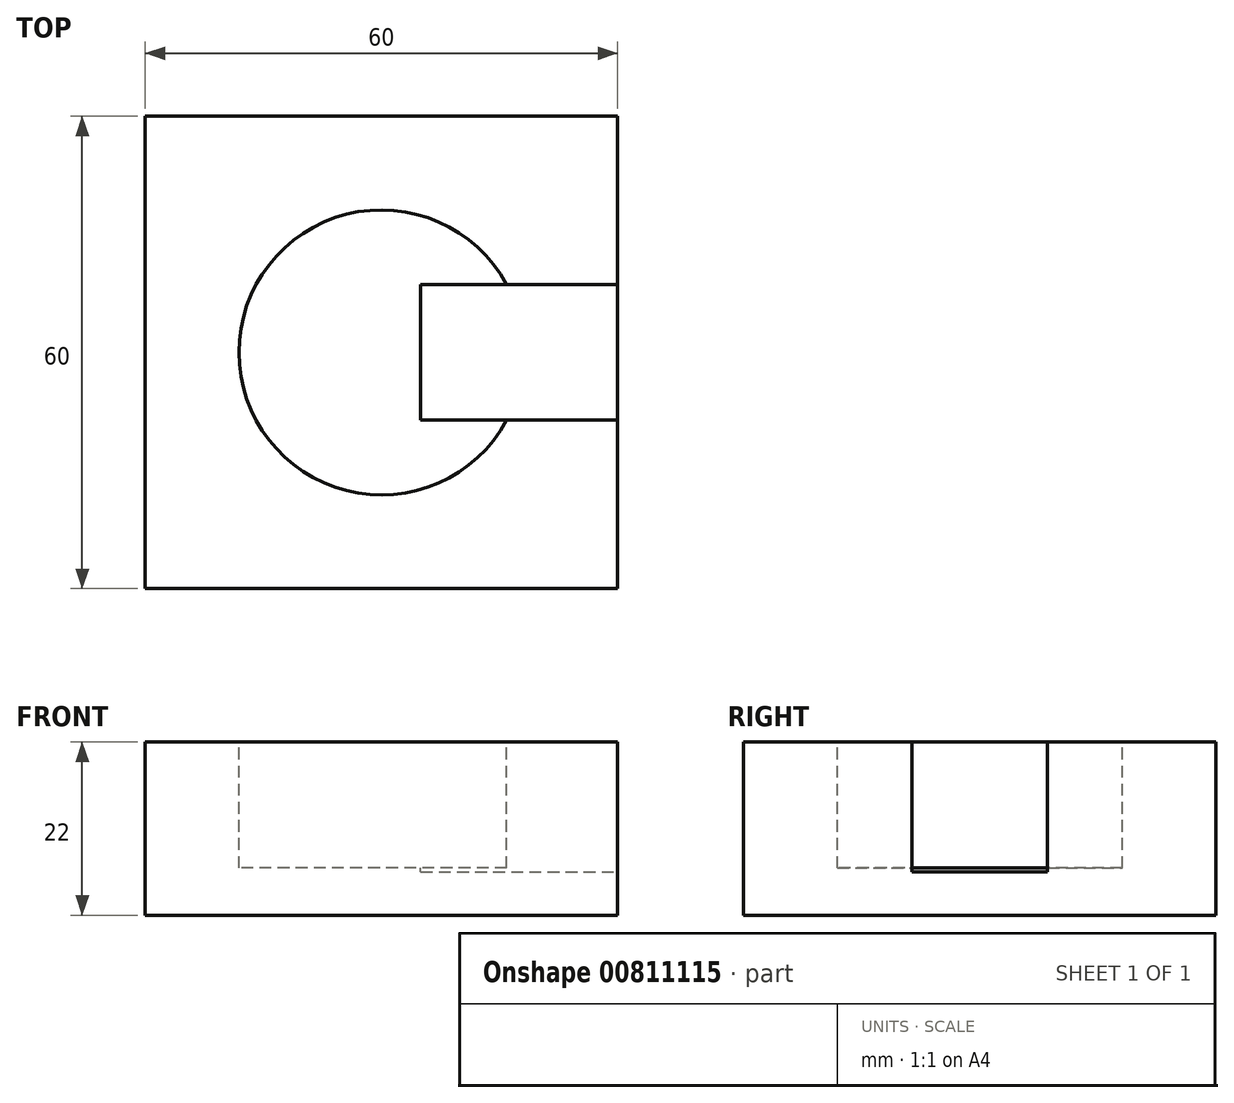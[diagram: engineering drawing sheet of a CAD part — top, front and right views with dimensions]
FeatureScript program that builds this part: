
annotation { "Feature Type Name" : "Feature", "Feature Type Description" : "" }
export const myFeature = defineFeature(function(context is Context, id is Id, definition is map)
    precondition{}
    {
        {
            var Q0;
            Q0=qCreatedBy(makeId("Top.planeOp"),FACE);
            var sketch = newSketch(context, id + "F0", { "sketchPlane" : qUnion([Q0])});
            skLineSegment(sketch, "E0.bottom", {"start": v(30, -30) * mm, "end": v(-30, -30) * mm});
            skLineSegment(sketch, "E0.top", {"start": v(30, 30) * mm, "end": v(-30, 30) * mm});
            skLineSegment(sketch, "E0.left", {"start": v(30, -30) * mm, "end": v(30, 30) * mm});
            skLineSegment(sketch, "E0.right", {"start": v(-30, -30) * mm, "end": v(-30, 30) * mm});
            skPoint(sketch, "E0.middle", {"position": v(0, 0) * mm});
            skSolve(sketch);
        }
        {
            var Q0;
            Q0=makeQuery(id+"F0.imprint","IMPRINT",FACE,{"disambiguationData":[TD([[makeQuery(id+"F0.imprint","IMPRINT",EDGE,{"derivedFrom":sQuery(id+"F0.wireOp",EDGE,"E0.bottom")}),-1.0]])]});
            extrude(context, id + "F1", {"entities" : qUnion([Q0]), "oppositeDirection" : true, "depth" : 22 * mm, "offsetDistance" : 25 * mm});
        }
        {
            var Q0;
            Q0=makeQuery(id+"F1.opExtrude","CAP_FACE",FACE,{"disambiguationData":[OSD([sQuery(id+"F0.wireOp",EDGE,"E0.bottom"),sQuery(id+"F0.wireOp",EDGE,"E0.top"),sQuery(id+"F0.wireOp",EDGE,"E0.left"),sQuery(id+"F0.wireOp",EDGE,"E0.right")])],"isStart":true});
            var sketch = newSketch(context, id + "F2", { "sketchPlane" : qUnion([Q0])});
            skCircle(sketch, "E1", {"center": v(0, 0) * mm, "radius": 18.1 * mm});
            skSolve(sketch);
        }
        {
            var Q0;
            Q0=makeQuery(id+"F2.imprint","IMPRINT",FACE,{"disambiguationData":[TD([[makeQuery(id+"F2.imprint","IMPRINT",EDGE,{"derivedFrom":sQuery(id+"F2.wireOp",EDGE,"E1")}),1.0]])]});
            extrude(context, id + "F3", {"entities" : qUnion([Q0]), "operationType" : NewBodyOperationType.REMOVE, "oppositeDirection" : true, "depth" : 16 * mm, "offsetDistance" : 25 * mm});
        }
        {
            var Q0;
            Q0=makeQuery(id+"F1.opExtrude","SWEPT_FACE",FACE,{"disambiguationData":[OSD([sQuery(id+"F0.wireOp",EDGE,"E0.left")])]});
            var sketch = newSketch(context, id + "F4", { "sketchPlane" : qUnion([Q0])});
            skLineSegment(sketch, "E2.bottom", {"start": v(8.62, -16.5) * mm, "end": v(-8.62, -16.5) * mm});
            skLineSegment(sketch, "E2.top", {"start": v(8.62, 8.13) * mm, "end": v(-8.62, 8.13) * mm});
            skLineSegment(sketch, "E2.left", {"start": v(8.62, -16.5) * mm, "end": v(8.62, 8.13) * mm});
            skLineSegment(sketch, "E2.right", {"start": v(-8.62, -16.5) * mm, "end": v(-8.62, 8.13) * mm});
            skPoint(sketch, "E2.middle", {"position": v(0, -4.19) * mm});
            skSolve(sketch);
        }
        {
            var Q0;
            {var subQ0=sQuery(id+"F4.wireOp",EDGE,"E2.bottom");Q0=makeQuery(id+"F4.imprint","IMPRINT",FACE,{"disambiguationData":[TD([[makeQuery(id+"F4.imprint","IMPRINT",EDGE,{"derivedFrom":subQ0}),-1.0]])]});}
            extrude(context, id + "F5", {"entities" : qUnion([Q0]), "operationType" : NewBodyOperationType.REMOVE, "oppositeDirection" : true, "depth" : 25 * mm, "offsetDistance" : 25 * mm});
        }
    });
